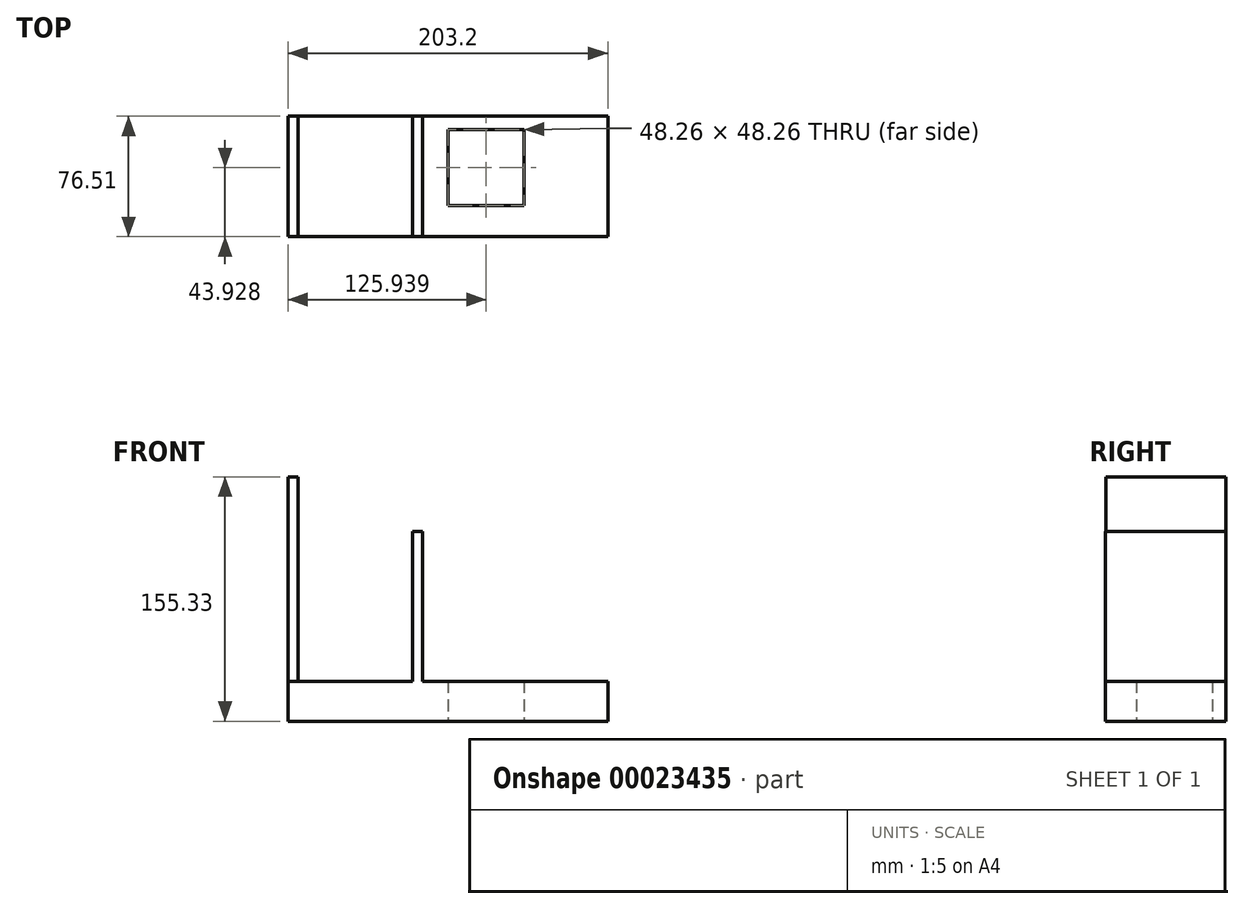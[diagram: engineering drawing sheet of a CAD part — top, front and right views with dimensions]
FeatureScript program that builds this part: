
annotation { "Feature Type Name" : "Feature", "Feature Type Description" : "" }
export const myFeature = defineFeature(function(context is Context, id is Id, definition is map)
    precondition{}
    {
        {
            var Q0;
            Q0=qCreatedBy(makeId("Top.planeOp"),FACE);
            var sketch = newSketch(context, id + "F0", { "sketchPlane" : qUnion([Q0])});
            skLineSegment(sketch, "E0.bottom", {"start": v(-85.58, 31.76) * mm, "end": v(117.62, 31.76) * mm});
            skLineSegment(sketch, "E0.top", {"start": v(-85.58, -44.75) * mm, "end": v(117.62, -44.75) * mm});
            skLineSegment(sketch, "E0.left", {"start": v(-85.58, 31.76) * mm, "end": v(-85.58, -44.75) * mm});
            skLineSegment(sketch, "E0.right", {"start": v(117.62, 31.76) * mm, "end": v(117.62, -44.75) * mm});
            skLineSegment(sketch, "E1.bottom", {"start": v(16.23, -24.95) * mm, "end": v(64.49, -24.95) * mm});
            skLineSegment(sketch, "E1.top", {"start": v(16.23, 23.3) * mm, "end": v(64.49, 23.3) * mm});
            skLineSegment(sketch, "E1.left", {"start": v(16.23, -24.95) * mm, "end": v(16.23, 23.3) * mm});
            skLineSegment(sketch, "E1.right", {"start": v(64.49, -24.95) * mm, "end": v(64.49, 23.3) * mm});
            skSolve(sketch);
        }
        {
            var Q0;
            Q0 = qSketchRegion(id + "F0", true);
            extrude(context, id + "F1", {"entities" : qUnion([Q0]), "depth" : 25.4 * mm});
        }
        {
            var Q0;
            Q0=makeQuery(id+"F1.opExtrude","SWEPT_FACE",FACE,{"disambiguationData":[OSD([sQuery(id+"F0.wireOp",EDGE,"E0.left")])]});
            var sketch = newSketch(context, id + "F2", { "sketchPlane" : qUnion([Q0])});
            skLineSegment(sketch, "E2.bottom", {"start": v(-31.76, 0) * mm, "end": v(44.56, 0) * mm});
            skLineSegment(sketch, "E2.top", {"start": v(-31.76, 155.33) * mm, "end": v(44.56, 155.33) * mm});
            skLineSegment(sketch, "E2.left", {"start": v(-31.76, 0) * mm, "end": v(-31.76, 155.33) * mm});
            skLineSegment(sketch, "E2.right", {"start": v(44.56, 0) * mm, "end": v(44.56, 155.33) * mm});
            skSolve(sketch);
        }
        {
            var Q0;
            Q0 = qSketchRegion(id + "F2", true);
            extrude(context, id + "F3", {"entities" : qUnion([Q0]), "operationType" : NewBodyOperationType.ADD, "oppositeDirection" : true, "depth" : 6.35 * mm});
        }
        {
            var Q0;
            Q0=makeQuery(id+"F1.opExtrude","CAP_FACE",FACE,{"disambiguationData":[OSD([sQuery(id+"F0.wireOp",EDGE,"E0.bottom"),sQuery(id+"F0.wireOp",EDGE,"E0.top"),sQuery(id+"F0.wireOp",EDGE,"E0.left"),sQuery(id+"F0.wireOp",EDGE,"E0.right"),sQuery(id+"F0.wireOp",EDGE,"E1.bottom"),sQuery(id+"F0.wireOp",EDGE,"E1.top"),sQuery(id+"F0.wireOp",EDGE,"E1.left"),sQuery(id+"F0.wireOp",EDGE,"E1.right")])],"isStart":false});
            var sketch = newSketch(context, id + "F4", { "sketchPlane" : qUnion([Q0])});
            skLineSegment(sketch, "E3.bottom", {"start": v(0, -44.75) * mm, "end": v(-6.35, -44.75) * mm});
            skLineSegment(sketch, "E3.top", {"start": v(0, 31.76) * mm, "end": v(-6.35, 31.76) * mm});
            skLineSegment(sketch, "E3.left", {"start": v(0, -44.75) * mm, "end": v(0, 31.76) * mm});
            skLineSegment(sketch, "E3.right", {"start": v(-6.35, -44.75) * mm, "end": v(-6.35, 31.76) * mm});
            skSolve(sketch);
        }
        {
            var Q0;
            Q0 = qSketchRegion(id + "F4", true);
            extrude(context, id + "F5", {"entities" : qUnion([Q0]), "operationType" : NewBodyOperationType.ADD, "depth" : 95.3 * mm});
        }
    });
